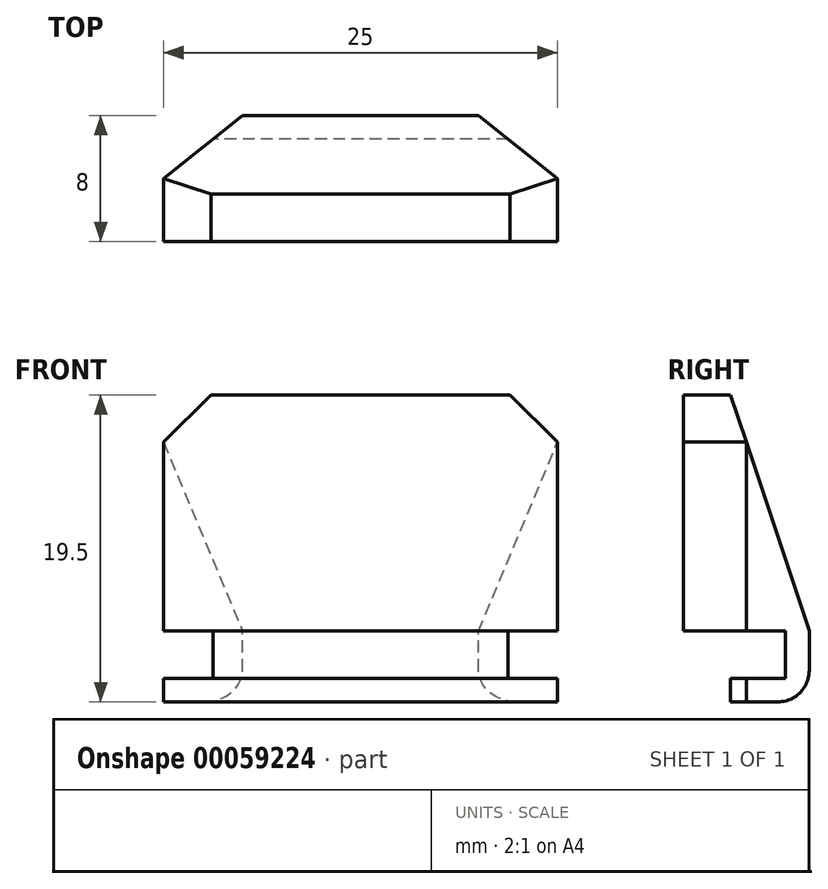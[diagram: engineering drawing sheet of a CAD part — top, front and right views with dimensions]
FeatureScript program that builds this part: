
annotation { "Feature Type Name" : "Feature", "Feature Type Description" : "" }
export const myFeature = defineFeature(function(context is Context, id is Id, definition is map)
    precondition{}
    {
        {
            var Q0;
            Q0=qCreatedBy(makeId("Right.planeOp"),FACE);
            var sketch = newSketch(context, id + "F2", { "sketchPlane" : qUnion([Q0])});
            skLineSegment(sketch, "E0.bottom", {"start": v(0, 0) * mm, "end": v(6.5, 0) * mm});
            skLineSegment(sketch, "E0.top", {"start": v(0, 15) * mm, "end": v(8, 15) * mm});
            skLineSegment(sketch, "E0.left", {"start": v(0, 0) * mm, "end": v(0, 15) * mm});
            skLineSegment(sketch, "E0.right", {"start": v(8, -4.5) * mm, "end": v(8, 15) * mm});
            skLineSegment(sketch, "E1.right", {"start": v(6.5, 0) * mm, "end": v(6.5, -3) * mm});
            skLineSegment(sketch, "E2.bottom", {"start": v(3, -4.5) * mm, "end": v(8, -4.5) * mm});
            skLineSegment(sketch, "E2.top", {"start": v(3, -3) * mm, "end": v(6.5, -3) * mm});
            skLineSegment(sketch, "E2.left", {"start": v(3, -4.5) * mm, "end": v(3, -3) * mm});
            skSolve(sketch);
        }
        {
            var Q0;
            Q0=makeQuery(id+"F2.imprint","IMPRINT",FACE,{"disambiguationData":[TD([[makeQuery(id+"F2.imprint","IMPRINT",EDGE,{"derivedFrom":sQuery(id+"F2.wireOp",EDGE,"E0.bottom")}),1.0]])]});
            extrude(context, id + "F3", {"entities" : qUnion([Q0]), "endBound" : BoundingType.SYMMETRIC, "depth" : 25 * mm});
        }
        {
            var Q0;
            Q0=makeQuery(id+"F3.opExtrude","SWEPT_FACE",FACE,{"disambiguationData":[OSD([sQuery(id+"F2.wireOp",EDGE,"E0.top")])]});
            var sketch = newSketch(context, id + "F0", { "sketchPlane" : qUnion([Q0])});
            skLineSegment(sketch, "E3", {"start": v(12.5, 4) * mm, "end": v(7.5, 8) * mm});
            skLineSegment(sketch, "E4", {"start": v(7.5, 8) * mm, "end": v(12.5, 8) * mm});
            skLineSegment(sketch, "E5", {"start": v(12.5, 4) * mm, "end": v(12.5, 8) * mm});
            skLineSegment(sketch, "E6", {"start": v(0, 8) * mm, "end": v(0, 0) * mm, "construction": true});
            skLineSegment(sketch, "E7.MirrorCS", {"start": v(-12.5, 4) * mm, "end": v(-7.5, 8) * mm});
            skLineSegment(sketch, "E8.MirrorCS", {"start": v(-7.5, 8) * mm, "end": v(-12.5, 8) * mm});
            skLineSegment(sketch, "E9.MirrorCS", {"start": v(-12.5, 4) * mm, "end": v(-12.5, 8) * mm});
            skSolve(sketch);
        }
        {
            var Q0;
            Q0=makeQuery(id+"F0.imprint","IMPRINT",FACE,{"disambiguationData":[TD([[makeQuery(id+"F0.imprint","IMPRINT",EDGE,{"derivedFrom":sQuery(id+"F0.wireOp",EDGE,"E3")}),-1.0]])]});
            var Q1;
            Q1=makeQuery(id+"F0.imprint","IMPRINT",FACE,{"disambiguationData":[TD([[makeQuery(id+"F0.imprint","IMPRINT",EDGE,{"derivedFrom":sQuery(id+"F0.wireOp",EDGE,"E7.MirrorCS")}),1.0]])]});
            extrude(context, id + "F1", {"entities" : qUnion([Q0, Q1]), "operationType" : NewBodyOperationType.REMOVE, "oppositeDirection" : true, "depth" : 25 * mm});
        }
        {
            var Q0;
            Q0=makeQuery(id+"F3.opExtrude","SWEPT_EDGE",EDGE,{"disambiguationData":[OSD([sQuery(id+"F2.wireOp",EDGE,"E0.top"),sQuery(id+"F2.wireOp",EDGE,"E0.right")])]});
            chamfer(context, id + "F4", {"entities" : qUnion([Q0]), "chamferType" : ChamferType.TWO_OFFSETS, "width1" : 5 * mm, "oppositeDirection" : false, "width2" : 15 * mm, "tangentPropagation" : true});
        }
        {
            var Q0;
            Q0=makeQuery(id+"F3.opExtrude","CAP_EDGE",EDGE,{"disambiguationData":[OSD([sQuery(id+"F2.wireOp",EDGE,"E0.top")])],"isStart":true});
            var Q1;
            Q1=makeQuery(id+"F3.opExtrude","CAP_EDGE",EDGE,{"disambiguationData":[OSD([sQuery(id+"F2.wireOp",EDGE,"E0.top")])],"isStart":false});
            chamfer(context, id + "F5", {"entities" : qUnion([Q0, Q1]), "width" : 3 * mm, "tangentPropagation" : true});
        }
        {
            var Q0;
            Q0=makeQuery(id+"F3.opExtrude","SWEPT_EDGE",EDGE,{"disambiguationData":[OSD([sQuery(id+"F2.wireOp",EDGE,"E0.right"),sQuery(id+"F2.wireOp",EDGE,"E2.bottom")])]});
            fillet(context, id + "F6", {"entities" : qUnion([Q0]), "radius" : 2 * mm, "tangentPropagation" : true, "allowEdgeOverflow" : false});
        }
    });
